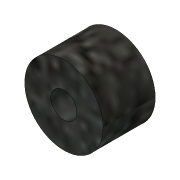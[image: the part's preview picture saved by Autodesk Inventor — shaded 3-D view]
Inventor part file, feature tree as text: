
AUTODESK INVENTOR PART (.ipt)
format: ipt  version: 2018.3 (Build 223284000, 284)  size: 100,352 bytes
history: native  units: in
note: dims shown in document units (in); Inventor stores cm internally (conversion verified against a paired STEP export)
features: extrude x1, sketch x1
ambient origin geometry x8: Origin, YZ Plane, XZ Plane, XY Plane, X Axis, Y Axis, Z Axis, Center Point
bodies: Solid1 (feature_tree)
feature tree (2):
  extrude  "Extrusion1"  Depth=0.25in
  sketch  "Sketch1"  dims[d0=0.125in d1=0.375in d2=0.25in d3=0.0in]
